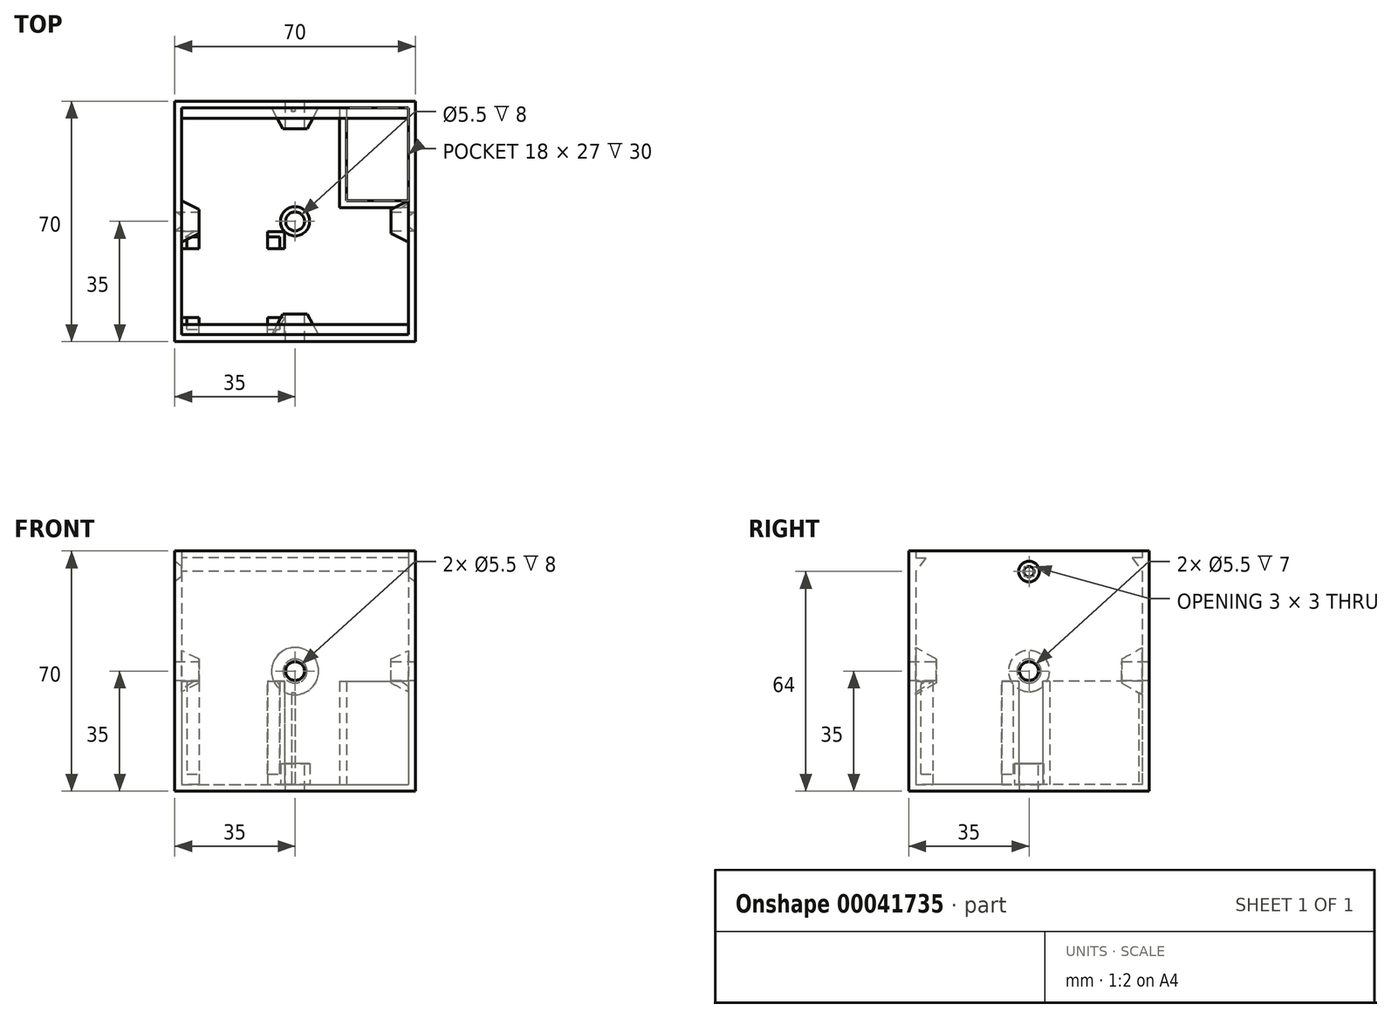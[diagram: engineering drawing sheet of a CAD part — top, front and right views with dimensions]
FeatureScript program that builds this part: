
annotation { "Feature Type Name" : "Feature", "Feature Type Description" : "" }
export const myFeature = defineFeature(function(context is Context, id is Id, definition is map)
    precondition{}
    {
        {
            var Q0;
            Q0=qCreatedBy(makeId("Top.planeOp"),FACE);
            var sketch = newSketch(context, id + "F0", { "sketchPlane" : qUnion([Q0])});
            skLineSegment(sketch, "E0.rect.bottom", {"start": v(35, 35) * mm, "end": v(-35, 35) * mm});
            skLineSegment(sketch, "E0.rect.top", {"start": v(35, -35) * mm, "end": v(-35, -35) * mm});
            skLineSegment(sketch, "E0.rect.left", {"start": v(35, 35) * mm, "end": v(35, -35) * mm});
            skLineSegment(sketch, "E0.rect.right", {"start": v(-35, 35) * mm, "end": v(-35, -35) * mm});
            skPoint(sketch, "E0.rect.middle", {"position": v(0, 0) * mm});
            skSolve(sketch);
        }
        {
            var Q0;
            Q0=qSketchRegion(id+"F0",true);
            extrude(context, id + "F1", {"entities" : qUnion([Q0]), "depth" : 2 * mm});
        }
        {
            var Q0;
            Q0=makeQuery(id+"F1.opExtrude","CAP_FACE",FACE,{"disambiguationData":[OSD([sQuery(id+"F0.wireOp",EDGE,"E0.rect.bottom"),sQuery(id+"F0.wireOp",EDGE,"E0.rect.top"),sQuery(id+"F0.wireOp",EDGE,"E0.rect.left"),sQuery(id+"F0.wireOp",EDGE,"E0.rect.right")])],"isStart":false});
            var sketch = newSketch(context, id + "F2", { "sketchPlane" : qUnion([Q0])});
            skLineSegment(sketch, "E1.rect.bottom", {"start": v(-35, 35) * mm, "end": v(35, 35) * mm});
            skLineSegment(sketch, "E1.rect.top", {"start": v(-35, -35) * mm, "end": v(35, -35) * mm});
            skLineSegment(sketch, "E1.rect.left", {"start": v(-35, 35) * mm, "end": v(-35, -35) * mm});
            skLineSegment(sketch, "E1.rect.right", {"start": v(35, 35) * mm, "end": v(35, -35) * mm});
            skPoint(sketch, "E1.rect.middle", {"position": v(0, 0) * mm});
            skLineSegment(sketch, "E2.rect.bottom", {"start": v(-33, 33) * mm, "end": v(33, 33) * mm});
            skLineSegment(sketch, "E2.rect.top", {"start": v(-33, -33) * mm, "end": v(33, -33) * mm});
            skLineSegment(sketch, "E2.rect.left", {"start": v(-33, 33) * mm, "end": v(-33, -33) * mm});
            skLineSegment(sketch, "E2.rect.right", {"start": v(33, 33) * mm, "end": v(33, -33) * mm});
            skSolve(sketch);
        }
        {
            var Q0;
            Q0=makeQuery(id+"F2.imprint","IMPRINT",FACE,{"disambiguationData":[TD([[makeQuery(id+"F2.imprint","IMPRINT",EDGE,{"derivedFrom":sQuery(id+"F2.wireOp",EDGE,"E2.rect.bottom")}),-1.0]])]});
            var sketch = newSketch(context, id + "F3", { "sketchPlane" : qUnion([Q0])});
            skPoint(sketch, "E3.0", {"position": v(-33, -33) * mm});
            skLineSegment(sketch, "E4.bottom", {"start": v(-33, -33) * mm, "end": v(-28, -33) * mm});
            skLineSegment(sketch, "E4.top", {"start": v(-33, -28) * mm, "end": v(-28, -28) * mm});
            skLineSegment(sketch, "E4.left", {"start": v(-33, -33) * mm, "end": v(-33, -28) * mm});
            skLineSegment(sketch, "E4.right", {"start": v(-28, -33) * mm, "end": v(-28, -28) * mm});
            skLineSegment(sketch, "E5", {"start": v(-28, -33) * mm, "end": v(-8, -33) * mm});
            skLineSegment(sketch, "E6.bottom", {"start": v(-8, -33) * mm, "end": v(-3, -33) * mm});
            skLineSegment(sketch, "E6.top", {"start": v(-8, -28) * mm, "end": v(-3, -28) * mm});
            skLineSegment(sketch, "E6.left", {"start": v(-8, -33) * mm, "end": v(-8, -28) * mm});
            skLineSegment(sketch, "E6.right", {"start": v(-3, -33) * mm, "end": v(-3, -28) * mm});
            skLineSegment(sketch, "E7", {"start": v(-3, -28) * mm, "end": v(-3, -8) * mm});
            skLineSegment(sketch, "E8.bottom", {"start": v(-3, -8) * mm, "end": v(-8, -8) * mm});
            skLineSegment(sketch, "E8.top", {"start": v(-3, -3) * mm, "end": v(-8, -3) * mm});
            skLineSegment(sketch, "E8.left", {"start": v(-3, -8) * mm, "end": v(-3, -3) * mm});
            skLineSegment(sketch, "E8.right", {"start": v(-8, -8) * mm, "end": v(-8, -3) * mm});
            skLineSegment(sketch, "E9", {"start": v(-8, -3) * mm, "end": v(-28, -3) * mm});
            skLineSegment(sketch, "E10.bottom", {"start": v(-28, -3) * mm, "end": v(-33, -3) * mm});
            skLineSegment(sketch, "E10.top", {"start": v(-28, -8) * mm, "end": v(-33, -8) * mm});
            skLineSegment(sketch, "E10.left", {"start": v(-28, -3) * mm, "end": v(-28, -8) * mm});
            skLineSegment(sketch, "E10.right", {"start": v(-33, -3) * mm, "end": v(-33, -8) * mm});
            skPoint(sketch, "E11.0", {"position": v(33, 33) * mm});
            skLineSegment(sketch, "E12", {"start": v(33, 33) * mm, "end": v(15, 33) * mm});
            skLineSegment(sketch, "E13", {"start": v(15, 33) * mm, "end": v(15, 6) * mm});
            skLineSegment(sketch, "E14", {"start": v(15, 6) * mm, "end": v(33, 6) * mm});
            skLineSegment(sketch, "E15.0", {"start": v(13, 4) * mm, "end": v(33, 4) * mm});
            skLineSegment(sketch, "E15.1", {"start": v(13, 33) * mm, "end": v(13, 4) * mm});
            skLineSegment(sketch, "E16", {"start": v(33, 6) * mm, "end": v(33, 4) * mm});
            skLineSegment(sketch, "E17", {"start": v(15, 33) * mm, "end": v(13, 33) * mm});
            skLineSegment(sketch, "E18.bottom", {"start": v(0, 33) * mm, "end": v(-1, 33) * mm});
            skLineSegment(sketch, "E18.top", {"start": v(0, 32) * mm, "end": v(-1, 32) * mm});
            skLineSegment(sketch, "E18.left", {"start": v(0, 33) * mm, "end": v(0, 32) * mm});
            skLineSegment(sketch, "E18.right", {"start": v(-1, 33) * mm, "end": v(-1, 32) * mm});
            skLineSegment(sketch, "E19", {"start": v(0, 0) * mm, "end": v(0, 32) * mm});
            skSolve(sketch);
        }
        {
            var Q0;
            Q0=qSketchRegion(id+"F3",true);
            extrude(context, id + "F4", {"entities" : qUnion([Q0]), "operationType" : NewBodyOperationType.ADD, "depth" : 30 * mm});
        }
        {
            var Q0;
            Q0=makeQuery(id+"F4.opExtrude","CAP_FACE",FACE,{"disambiguationData":[OSD([sQuery(id+"F3.wireOp",EDGE,"E4.bottom"),sQuery(id+"F3.wireOp",EDGE,"E4.top"),sQuery(id+"F3.wireOp",EDGE,"E4.left"),sQuery(id+"F3.wireOp",EDGE,"E4.right")])],"isStart":false});
            var sketch = newSketch(context, id + "F5", { "sketchPlane" : qUnion([Q0])});
            skLineSegment(sketch, "E20", {"start": v(-33, -33) * mm, "end": v(-31.5, -33) * mm});
            skLineSegment(sketch, "E21", {"start": v(-31.5, -33) * mm, "end": v(-31.5, -31.5) * mm});
            skLineSegment(sketch, "E22.bottom", {"start": v(-31.5, -31.5) * mm, "end": v(-4.5, -31.5) * mm});
            skLineSegment(sketch, "E22.top", {"start": v(-31.5, -4.5) * mm, "end": v(-4.5, -4.5) * mm});
            skLineSegment(sketch, "E22.left", {"start": v(-31.5, -31.5) * mm, "end": v(-31.5, -4.5) * mm});
            skLineSegment(sketch, "E22.right", {"start": v(-4.5, -31.5) * mm, "end": v(-4.5, -4.5) * mm});
            skSolve(sketch);
        }
        {
            var Q0;
            Q0=qSketchRegion(id+"F5",true);
            extrude(context, id + "F6", {"entities" : qUnion([Q0]), "operationType" : NewBodyOperationType.REMOVE, "oppositeDirection" : true, "depth" : 27 * mm});
        }
        {
            var Q0;
            Q0=makeQuery(id+"F1.opExtrude","CAP_FACE",FACE,{"disambiguationData":[OSD([sQuery(id+"F0.wireOp",EDGE,"E0.rect.bottom"),sQuery(id+"F0.wireOp",EDGE,"E0.rect.top"),sQuery(id+"F0.wireOp",EDGE,"E0.rect.left"),sQuery(id+"F0.wireOp",EDGE,"E0.rect.right")])],"isStart":false});
            var sketch = newSketch(context, id + "F7", { "sketchPlane" : qUnion([Q0])});
            skCircle(sketch, "E23", {"center": v(0, 0) * mm, "radius": 4.25 * mm});
            skSolve(sketch);
        }
        {
            var Q0;
            Q0=qSketchRegion(id+"F7",true);
            extrude(context, id + "F8", {"entities" : qUnion([Q0]), "operationType" : NewBodyOperationType.ADD, "depth" : 6 * mm});
        }
        {
            var Q0;
            Q0=makeQuery(id+"F8.opExtrude","CAP_FACE",FACE,{"disambiguationData":[OSD([sQuery(id+"F7.wireOp",EDGE,"E23")])],"isStart":false});
            var sketch = newSketch(context, id + "F9", { "sketchPlane" : qUnion([Q0])});
            skCircle(sketch, "E24", {"center": v(0, 0) * mm, "radius": 2.75 * mm});
            skSolve(sketch);
        }
        {
            var Q0;
            Q0=qSketchRegion(id+"F9",true);
            extrude(context, id + "F10", {"entities" : qUnion([Q0]), "operationType" : NewBodyOperationType.REMOVE, "endBound" : BoundingType.THROUGH_ALL, "oppositeDirection" : true, "depth" : 25 * mm});
        }
        {
            var Q0;
            Q0=qSketchRegion(id+"F2",true);
            extrude(context, id + "F11", {"entities" : qUnion([Q0]), "operationType" : NewBodyOperationType.ADD, "depth" : 68 * mm});
        }
        {
            var Q0;
            Q0=qCreatedBy(makeId("Front.planeOp"),FACE);
            var sketch = newSketch(context, id + "F12", { "sketchPlane" : qUnion([Q0])});
            skLineSegment(sketch, "E25", {"start": v(0, 0) * mm, "end": v(0, 35) * mm});
            skLineSegment(sketch, "E26", {"start": v(0, 35) * mm, "end": v(-35, 35) * mm});
            skLineSegment(sketch, "E27", {"start": v(-35, 35) * mm, "end": v(-35, 42) * mm});
            skLineSegment(sketch, "E28", {"start": v(-35, 35) * mm, "end": v(-28, 35) * mm});
            skLineSegment(sketch, "E29", {"start": v(-28, 35) * mm, "end": v(-28, 38.5) * mm});
            skLineSegment(sketch, "E30", {"start": v(-35, 42) * mm, "end": v(-28, 38.5) * mm});
            skLineSegment(sketch, "E31.MirrorCS", {"start": v(28, 35) * mm, "end": v(28, 38.5) * mm});
            skLineSegment(sketch, "E32.MirrorCS", {"start": v(35, 35) * mm, "end": v(28, 35) * mm});
            skLineSegment(sketch, "E33.MirrorCS", {"start": v(35, 35) * mm, "end": v(35, 42) * mm});
            skLineSegment(sketch, "E34.MirrorCS", {"start": v(35, 42) * mm, "end": v(28, 38.5) * mm});
            skSolve(sketch);
        }
        {
            var Q0;
            Q0=qSketchRegion(id+"F12",true);
            var Q1;
            Q1=sQuery(id+"F12.wireOp",EDGE,"E26");
            revolve(context, id + "F13", {"operationType" : NewBodyOperationType.ADD, "entities" : qUnion([Q0]), "axis" : qUnion([Q1]), "revolveType" : RevolveType.FULL});
        }
        {
            var Q0;
            Q0=qCreatedBy(makeId("Right.planeOp"),FACE);
            var sketch = newSketch(context, id + "F14", { "sketchPlane" : qUnion([Q0])});
            skLineSegment(sketch, "E35", {"start": v(0, 0) * mm, "end": v(0, 35) * mm});
            skLineSegment(sketch, "E36", {"start": v(0, 35) * mm, "end": v(-35, 35) * mm});
            skLineSegment(sketch, "E37", {"start": v(-35, 35) * mm, "end": v(-35, 43) * mm});
            skLineSegment(sketch, "E38", {"start": v(-35, 43) * mm, "end": v(-27, 38.5) * mm});
            skLineSegment(sketch, "E39", {"start": v(-27, 38.5) * mm, "end": v(-27, 35) * mm});
            skLineSegment(sketch, "E40", {"start": v(-27, 35) * mm, "end": v(-35, 35) * mm});
            skLineSegment(sketch, "E41.MirrorCS", {"start": v(27, 35) * mm, "end": v(35, 35) * mm});
            skLineSegment(sketch, "E42.MirrorCS", {"start": v(27, 38.5) * mm, "end": v(27, 35) * mm});
            skLineSegment(sketch, "E43.MirrorCS", {"start": v(35, 43) * mm, "end": v(27, 38.5) * mm});
            skLineSegment(sketch, "E44.MirrorCS", {"start": v(35, 35) * mm, "end": v(35, 43) * mm});
            skSolve(sketch);
        }
        {
            var Q0;
            Q0=qSketchRegion(id+"F14",true);
            var Q1;
            Q1=sQuery(id+"F14.wireOp",EDGE,"E36");
            revolve(context, id + "F15", {"operationType" : NewBodyOperationType.ADD, "entities" : qUnion([Q0]), "axis" : qUnion([Q1]), "revolveType" : RevolveType.FULL});
        }
        {
            var Q0;
            Q0=makeQuery(id+"F15.opRevolve","SWEPT_FACE",FACE,{"disambiguationData":[OSD([sQuery(id+"F14.wireOp",EDGE,"E39")])]});
            var sketch = newSketch(context, id + "F16", { "sketchPlane" : qUnion([Q0])});
            skCircle(sketch, "E45", {"center": v(0, 35) * mm, "radius": 2.75 * mm});
            skSolve(sketch);
        }
        {
            var Q0;
            Q0=qSketchRegion(id+"F16",true);
            extrude(context, id + "F17", {"entities" : qUnion([Q0]), "operationType" : NewBodyOperationType.REMOVE, "endBound" : BoundingType.THROUGH_ALL, "oppositeDirection" : true, "depth" : 25 * mm, "hasSecondDirection" : true, "secondDirectionBound" : SecondDirectionBoundingType.THROUGH_ALL, "secondDirectionOppositeDirection" : false, "secondDirectionDepth" : 25 * mm});
        }
        {
            var Q0;
            Q0=makeQuery(id+"F13.opRevolve","SWEPT_FACE",FACE,{"disambiguationData":[OSD([sQuery(id+"F12.wireOp",EDGE,"E29")])]});
            var sketch = newSketch(context, id + "F18", { "sketchPlane" : qUnion([Q0])});
            skCircle(sketch, "E46", {"center": v(0, 35) * mm, "radius": 2.75 * mm});
            skSolve(sketch);
        }
        {
            var Q0;
            Q0=qSketchRegion(id+"F18",true);
            extrude(context, id + "F19", {"entities" : qUnion([Q0]), "operationType" : NewBodyOperationType.REMOVE, "endBound" : BoundingType.THROUGH_ALL, "oppositeDirection" : true, "depth" : 25 * mm, "hasSecondDirection" : true, "secondDirectionBound" : SecondDirectionBoundingType.THROUGH_ALL, "secondDirectionOppositeDirection" : false, "secondDirectionDepth" : 25 * mm});
        }
        {
            var Q0;
            Q0=makeQuery(id+"F11.opExtrude","SWEPT_FACE",FACE,{"disambiguationData":[OSD([sQuery(id+"F2.wireOp",EDGE,"E2.rect.left")])]});
            var sketch = newSketch(context, id + "F20", { "sketchPlane" : qUnion([Q0])});
            skLineSegment(sketch, "E47", {"start": v(-33, 70) * mm, "end": v(-33, 68) * mm});
            skLineSegment(sketch, "E48", {"start": v(-33, 68) * mm, "end": v(-30, 68) * mm});
            skLineSegment(sketch, "E49", {"start": v(-30, 68) * mm, "end": v(-33, 64) * mm});
            skLineSegment(sketch, "E50", {"start": v(-33, 64) * mm, "end": v(-33, 68) * mm});
            skLineSegment(sketch, "E51", {"start": v(0, 70) * mm, "end": v(0, 64) * mm});
            skLineSegment(sketch, "E52.MirrorCS", {"start": v(30, 68) * mm, "end": v(33, 64) * mm});
            skLineSegment(sketch, "E53.MirrorCS", {"start": v(33, 68) * mm, "end": v(30, 68) * mm});
            skLineSegment(sketch, "E54.MirrorCS", {"start": v(33, 64) * mm, "end": v(33, 68) * mm});
            skSolve(sketch);
        }
        {
            var Q0;
            Q0=qSketchRegion(id+"F20",true);
            extrude(context, id + "F21", {"entities" : qUnion([Q0]), "operationType" : NewBodyOperationType.ADD, "endBound" : BoundingType.UP_TO_NEXT, "depth" : 25 * mm});
        }
        {
            var Q0;
            Q0=makeQuery(id+"F11.opExtrude","SWEPT_FACE",FACE,{"disambiguationData":[OSD([sQuery(id+"F2.wireOp",EDGE,"E2.rect.left")])]});
            var sketch = newSketch(context, id + "F22", { "sketchPlane" : qUnion([Q0])});
            skLineSegment(sketch, "E55", {"start": v(0, 70) * mm, "end": v(0, 64) * mm});
            skCircle(sketch, "E56", {"center": v(0, 64) * mm, "radius": 1.5 * mm});
            skSolve(sketch);
        }
        {
            var Q0;
            Q0=makeQuery(id+"F11.boolean.opBoolean","MERGE",FACE,{"derivedFrom":[makeQuery(id+"F1.opExtrude","SWEPT_FACE",FACE,{"disambiguationData":[OSD([sQuery(id+"F0.wireOp",EDGE,"E0.rect.right")])]}),makeQuery(id+"F11.opExtrude","SWEPT_FACE",FACE,{"disambiguationData":[OSD([sQuery(id+"F2.wireOp",EDGE,"E1.rect.left")])]})]});
            var sketch = newSketch(context, id + "F23", { "sketchPlane" : qUnion([Q0])});
            skLineSegment(sketch, "E57", {"start": v(0, 70) * mm, "end": v(0, 64) * mm});
            skCircle(sketch, "E58", {"center": v(0, 64) * mm, "radius": 3 * mm});
            skSolve(sketch);
        }
        {
            var Q1;
            Q1=makeQuery(id+"F22.imprint","IMPRINT",FACE,{"disambiguationData":[TD([[makeQuery(id+"F22.imprint","IMPRINT",EDGE,{"derivedFrom":sQuery(id+"F22.wireOp",EDGE,"E56")}),1.0]])]});
            var Q2;
            Q2=makeQuery(id+"F23.imprint","IMPRINT",FACE,{"disambiguationData":[TD([[makeQuery(id+"F23.imprint","IMPRINT",EDGE,{"derivedFrom":sQuery(id+"F23.wireOp",EDGE,"E58")}),1.0]])]});
            loft(context, id + "F24", {"operationType" : NewBodyOperationType.REMOVE, "sheetProfilesArray" : [{ "sheetProfileEntities" : qUnion([Q1]) }, { "sheetProfileEntities" : qUnion([Q2]) }]});
        }
        {
            var Q0;
            Q0=makeQuery(id+"F11.opExtrude","SWEPT_FACE",FACE,{"disambiguationData":[OSD([sQuery(id+"F2.wireOp",EDGE,"E2.rect.right")])]});
            var sketch = newSketch(context, id + "F25", { "sketchPlane" : qUnion([Q0])});
            skLineSegment(sketch, "E59", {"start": v(0, 70) * mm, "end": v(0, 64) * mm});
            skCircle(sketch, "E60", {"center": v(0, 64) * mm, "radius": 1.5 * mm});
            skSolve(sketch);
        }
        {
            var Q0;
            Q0=makeQuery(id+"F11.boolean.opBoolean","MERGE",FACE,{"derivedFrom":[makeQuery(id+"F1.opExtrude","SWEPT_FACE",FACE,{"disambiguationData":[OSD([sQuery(id+"F0.wireOp",EDGE,"E0.rect.left")])]}),makeQuery(id+"F11.opExtrude","SWEPT_FACE",FACE,{"disambiguationData":[OSD([sQuery(id+"F2.wireOp",EDGE,"E1.rect.right")])]})]});
            var sketch = newSketch(context, id + "F26", { "sketchPlane" : qUnion([Q0])});
            skLineSegment(sketch, "E61", {"start": v(0, 70) * mm, "end": v(0, 64) * mm});
            skCircle(sketch, "E62", {"center": v(0, 64) * mm, "radius": 3 * mm});
            skSolve(sketch);
        }
        {
            var Q0;
            Q0=makeQuery(id+"F26.imprint","IMPRINT",FACE,{"disambiguationData":[TD([[makeQuery(id+"F26.imprint","IMPRINT",EDGE,{"derivedFrom":sQuery(id+"F26.wireOp",EDGE,"E62")}),1.0]])]});
            var Q1;
            Q1=makeQuery(id+"F25.imprint","IMPRINT",FACE,{"disambiguationData":[TD([[makeQuery(id+"F25.imprint","IMPRINT",EDGE,{"derivedFrom":sQuery(id+"F25.wireOp",EDGE,"E60")}),1.0]])]});
            loft(context, id + "F27", {"operationType" : NewBodyOperationType.REMOVE, "sheetProfilesArray" : [{ "sheetProfileEntities" : qUnion([Q0]) }, { "sheetProfileEntities" : qUnion([Q1]) }]});
        }
    });
